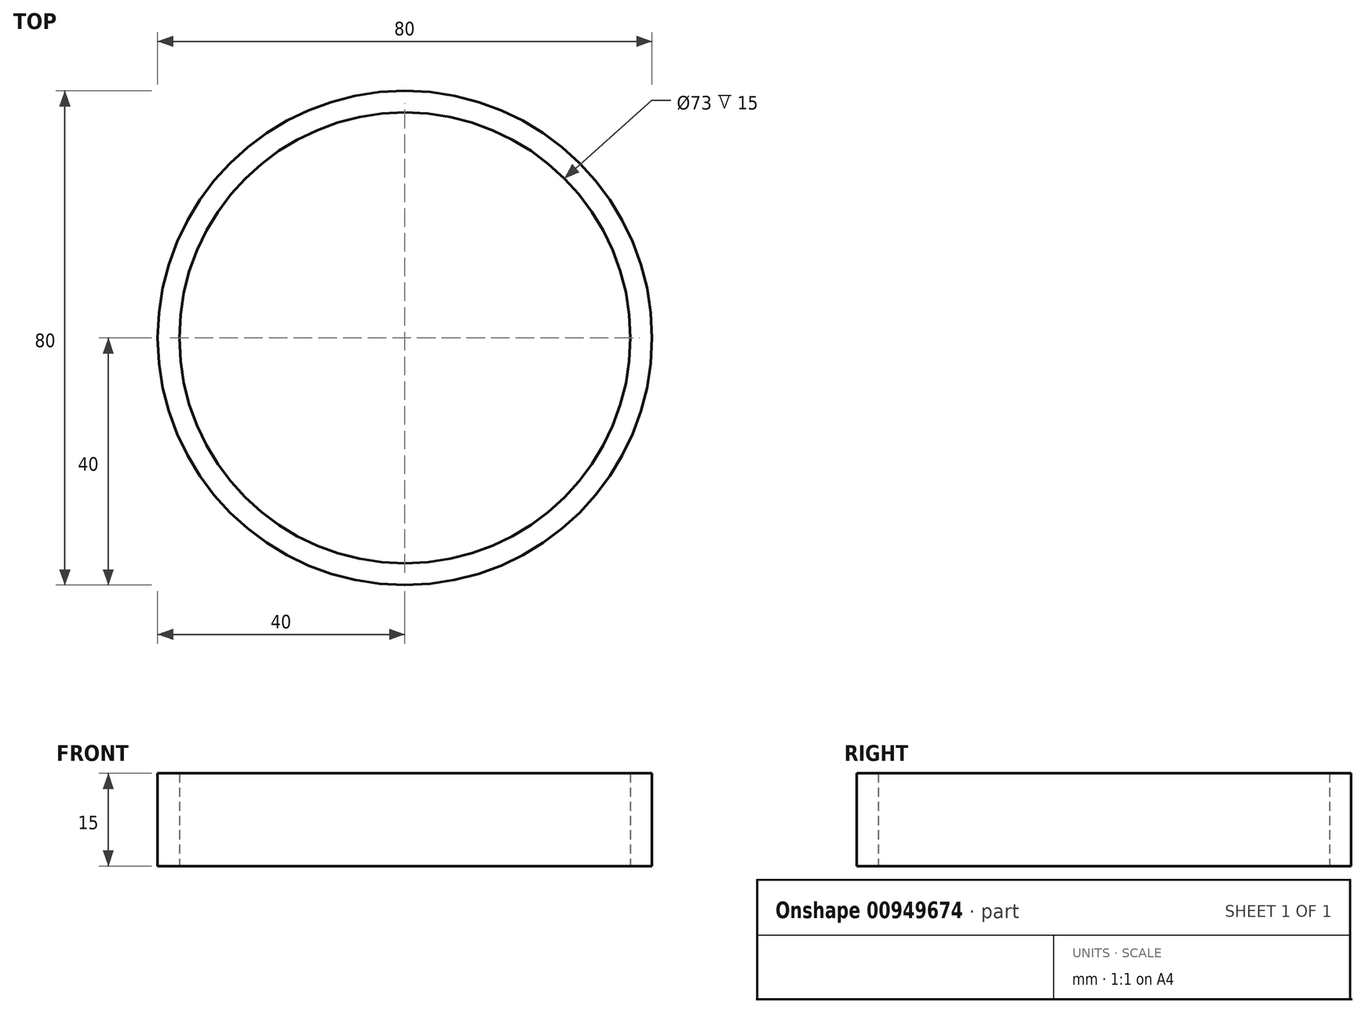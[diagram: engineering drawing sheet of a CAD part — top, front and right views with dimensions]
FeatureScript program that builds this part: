
annotation { "Feature Type Name" : "Feature", "Feature Type Description" : "" }
export const myFeature = defineFeature(function(context is Context, id is Id, definition is map)
    precondition{}
    {
        {
            var Q0;
            Q0=qCreatedBy(makeId("Top.planeOp"),FACE);
            var sketch = newSketch(context, id + "F0", { "sketchPlane" : qUnion([Q0])});
            skCircle(sketch, "E0", {"center": v(0, 0) * mm, "radius": 40 * mm});
            skCircle(sketch, "E1", {"center": v(0, 0) * mm, "radius": 36.5 * mm});
            skLineSegment(sketch, "E2", {"start": v(0, 0) * mm, "end": v(0, 140) * mm, "construction": true});
            skLineSegment(sketch, "E3", {"start": v(0, 0) * mm, "end": v(-121.24, -70) * mm, "construction": true});
            skLineSegment(sketch, "E4", {"start": v(0, 0) * mm, "end": v(121.24, -70) * mm, "construction": true});
            skLineSegment(sketch, "E5", {"start": v(106.43, -95.65) * mm, "end": v(121.24, -70) * mm, "construction": true});
            skLineSegment(sketch, "E6", {"start": v(24.98, -136.73) * mm, "end": v(125.54, 37.44) * mm, "construction": true});
            skArc(sketch, "E7", {"start": v(58.12, -79.33) * mm, "mid": v(91.94, -89.92) * mm, "end": v(121.24, -70) * mm});
            skLineSegment(sketch, "E8", {"start": v(85.99, -49.64) * mm, "end": v(121.24, -70) * mm, "construction": true});
            skPoint(sketch, "E9", {"position": v(77.94, -45) * mm});
            skLineSegment(sketch, "E10", {"start": v(0, 0) * mm, "end": v(45.47, 26.25) * mm, "construction": true});
            skArc(sketch, "E11", {"start": v(97.76, -10.67) * mm, "mid": v(68.62, 3.55) * mm, "end": v(45.47, 26.25) * mm});
            skLineSegment(sketch, "E12", {"start": v(0, 0) * mm, "end": v(0, -76.26) * mm, "construction": true});
            skPoint(sketch, "E13", {"position": v(0, -52.5) * mm});
            skArc(sketch, "E14", {"start": v(58.12, -79.33) * mm, "mid": v(31.24, -61.2) * mm, "end": v(0, -52.5) * mm});
            skLineSegment(sketch, "E15", {"start": v(121.24, -70) * mm, "end": v(132.4, -50.68) * mm, "construction": true});
            skArc(sketch, "E16", {"start": v(121.24, -70) * mm, "mid": v(123.84, -34.66) * mm, "end": v(97.76, -10.67) * mm});
            skArc(sketch, "E17.MirrorCS", {"start": v(0, 140) * mm, "mid": v(31.9, 124.58) * mm, "end": v(39.64, 90) * mm});
            skArc(sketch, "E18.MirrorCS", {"start": v(39.64, 90) * mm, "mid": v(37.39, 57.65) * mm, "end": v(45.47, 26.25) * mm});
            skArc(sketch, "E19.MirrorCS", {"start": v(-39.64, 90) * mm, "mid": v(-37.39, 57.65) * mm, "end": v(-45.47, 26.25) * mm});
            skArc(sketch, "E20.MirrorCS", {"start": v(-39.64, 90) * mm, "mid": v(-31.9, 124.58) * mm, "end": v(0, 140) * mm});
            skArc(sketch, "E21.MirrorCS", {"start": v(-97.76, -10.67) * mm, "mid": v(-68.62, 3.55) * mm, "end": v(-45.47, 26.25) * mm});
            skArc(sketch, "E22.MirrorCS", {"start": v(-121.24, -70) * mm, "mid": v(-123.84, -34.66) * mm, "end": v(-97.76, -10.67) * mm});
            skArc(sketch, "E23.MirrorCS", {"start": v(-58.12, -79.33) * mm, "mid": v(-31.24, -61.2) * mm, "end": v(0, -52.5) * mm});
            skArc(sketch, "E24.MirrorCS", {"start": v(-58.12, -79.33) * mm, "mid": v(-91.94, -89.92) * mm, "end": v(-121.24, -70) * mm});
            skPoint(sketch, "E25", {"position": v(75.26, -49.64) * mm});
            skSolve(sketch);
        }
        {
            var Q0;
            Q0=makeQuery(id+"F0.imprint","IMPRINT",FACE,{"disambiguationData":[TD([[makeQuery(id+"F0.imprint","IMPRINT",EDGE,{"derivedFrom":sQuery(id+"F0.wireOp",EDGE,"E0")}),1.0]])]});
            extrude(context, id + "F1", {"entities" : qUnion([Q0]), "depth" : 15 * mm, "offsetDistance" : 25 * mm});
        }
    });
